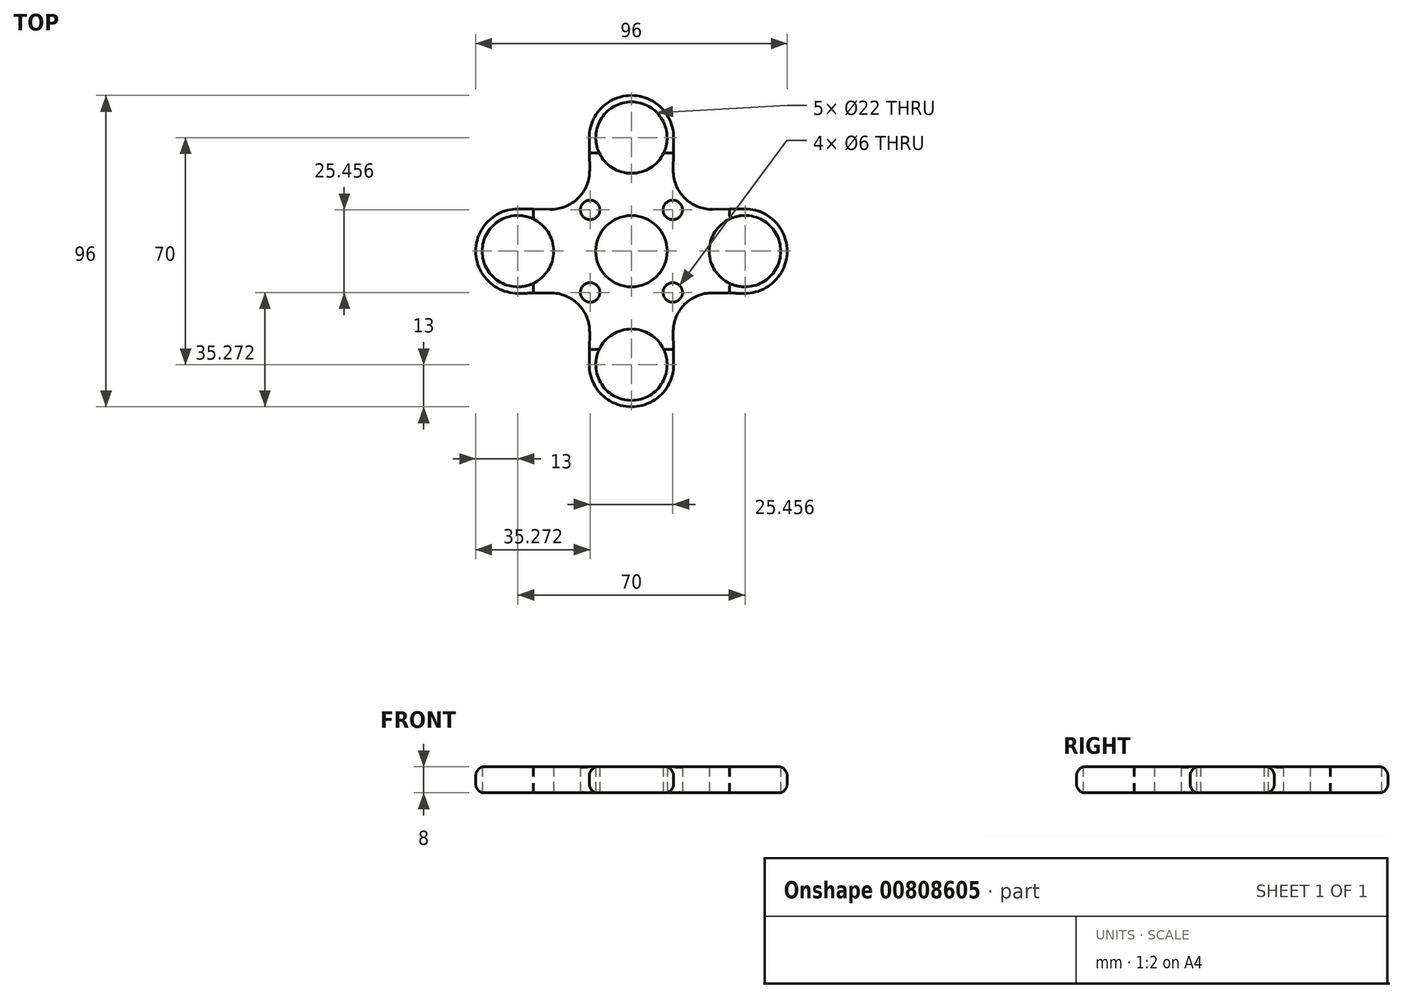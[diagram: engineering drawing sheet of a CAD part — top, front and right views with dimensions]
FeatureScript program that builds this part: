
annotation { "Feature Type Name" : "Feature", "Feature Type Description" : "" }
export const myFeature = defineFeature(function(context is Context, id is Id, definition is map)
    precondition{}
    {
        {
            var Q0;
            Q0=qCreatedBy(makeId("Top.planeOp"),FACE);
            var sketch = newSketch(context, id + "F0", { "sketchPlane" : qUnion([Q0])});
            skCircle(sketch, "E0", {"center": v(0, 0) * mm, "radius": 11 * mm});
            skLineSegment(sketch, "E1", {"start": v(0, 0) * mm, "end": v(0, 35) * mm});
            skCircle(sketch, "E2", {"center": v(0, 35) * mm, "radius": 11 * mm});
            skLineSegment(sketch, "E3", {"start": v(0, 0) * mm, "end": v(0, -35) * mm});
            skCircle(sketch, "E4", {"center": v(0, -35) * mm, "radius": 11 * mm});
            skLineSegment(sketch, "E5", {"start": v(0, 0) * mm, "end": v(-35, 0) * mm});
            skCircle(sketch, "E6", {"center": v(-35, 0) * mm, "radius": 11 * mm});
            skLineSegment(sketch, "E7", {"start": v(0, 0) * mm, "end": v(35, 0) * mm});
            skCircle(sketch, "E8", {"center": v(35, 0) * mm, "radius": 11 * mm});
            skLineSegment(sketch, "E9", {"start": v(-11.16, -11.31) * mm, "end": v(-11.31, -11.16) * mm});
            skLineSegment(sketch, "E10", {"start": v(11.16, 11.31) * mm, "end": v(11.31, 11.16) * mm});
            skLineSegment(sketch, "E11", {"start": v(11.31, -11.16) * mm, "end": v(11.16, -11.31) * mm});
            skLineSegment(sketch, "E12", {"start": v(0, 0) * mm, "end": v(12.73, -12.73) * mm});
            skLineSegment(sketch, "E13", {"start": v(0, 0) * mm, "end": v(-12.73, -12.73) * mm});
            skLineSegment(sketch, "E14", {"start": v(0, 0) * mm, "end": v(-12.73, 12.73) * mm});
            skLineSegment(sketch, "E15", {"start": v(0, 0) * mm, "end": v(12.73, 12.73) * mm});
            skCircle(sketch, "E16", {"center": v(12.73, -12.73) * mm, "radius": 3 * mm});
            skLineSegment(sketch, "E17", {"start": v(12.73, -12.73) * mm, "end": v(14.85, -10.6) * mm});
            skLineSegment(sketch, "E18", {"start": v(12.73, -12.73) * mm, "end": v(10.6, -10.6) * mm});
            skCircle(sketch, "E19", {"center": v(35, 0) * mm, "radius": 13 * mm});
            skCircle(sketch, "E20", {"center": v(12.73, 12.73) * mm, "radius": 3 * mm});
            skCircle(sketch, "E21", {"center": v(0, 35) * mm, "radius": 13 * mm});
            skLineSegment(sketch, "E22", {"start": v(12.88, 25.02) * mm, "end": v(13, 34.84) * mm});
            skLineSegment(sketch, "E23", {"start": v(25.02, 12.88) * mm, "end": v(34.84, 13) * mm});
            skArc(sketch, "E24.filletArc", {"start": v(12.88, 25.02) * mm, "mid": v(16.4, 16.4) * mm, "end": v(25.02, 12.88) * mm});
            skCircle(sketch, "E25", {"center": v(0, -35) * mm, "radius": 13 * mm});
            skCircle(sketch, "E26", {"center": v(-12.73, -12.73) * mm, "radius": 3 * mm});
            skCircle(sketch, "E27", {"center": v(-12.73, 12.73) * mm, "radius": 3 * mm});
            skCircle(sketch, "E28", {"center": v(-35, 0) * mm, "radius": 13 * mm});
            skLineSegment(sketch, "E29", {"start": v(-25.02, 12.88) * mm, "end": v(-34.84, 13) * mm});
            skLineSegment(sketch, "E30", {"start": v(-12.88, 25.02) * mm, "end": v(-13, 34.84) * mm});
            skArc(sketch, "E31.filletArc", {"start": v(-25.02, 12.88) * mm, "mid": v(-16.4, 16.4) * mm, "end": v(-12.88, 25.02) * mm});
            skLineSegment(sketch, "E32", {"start": v(-25.02, -12.88) * mm, "end": v(-34.84, -13) * mm});
            skLineSegment(sketch, "E33", {"start": v(-12.88, -25.02) * mm, "end": v(-13, -34.84) * mm});
            skArc(sketch, "E34.filletArc", {"start": v(-12.88, -25.02) * mm, "mid": v(-16.4, -16.4) * mm, "end": v(-25.02, -12.88) * mm});
            skLineSegment(sketch, "E35", {"start": v(12.88, -25.02) * mm, "end": v(13, -34.84) * mm});
            skLineSegment(sketch, "E36", {"start": v(25.02, -12.88) * mm, "end": v(34.84, -13) * mm});
            skArc(sketch, "E37.filletArc", {"start": v(25.02, -12.88) * mm, "mid": v(16.4, -16.4) * mm, "end": v(12.88, -25.02) * mm});
            skSolve(sketch);
        }
        {
            var Q0;
            Q0 = qSketchRegion(id + "F0", true);
            extrude(context, id + "F1", {"entities" : qUnion([Q0]), "depth" : 8 * mm, "offsetDistance" : 25 * mm});
        }
        {
            var Q0;
            Q0=makeQuery(id+"F1.opExtrude","CAP_EDGE",EDGE,{"disambiguationData":[OSD([sQuery(id+"F0.wireOp",EDGE,"E37.filletArc")])],"isStart":true});
            var Q1;
            Q1=makeQuery(id+"F1.opExtrude","CAP_EDGE",EDGE,{"disambiguationData":[OSD([sQuery(id+"F0.wireOp",EDGE,"E31.filletArc")])],"isStart":false});
            fillet(context, id + "F2", {"entities" : qUnion([Q0, Q1]), "radius" : 3 * mm, "tangentPropagation" : true, "allowEdgeOverflow" : false});
        }
    });
